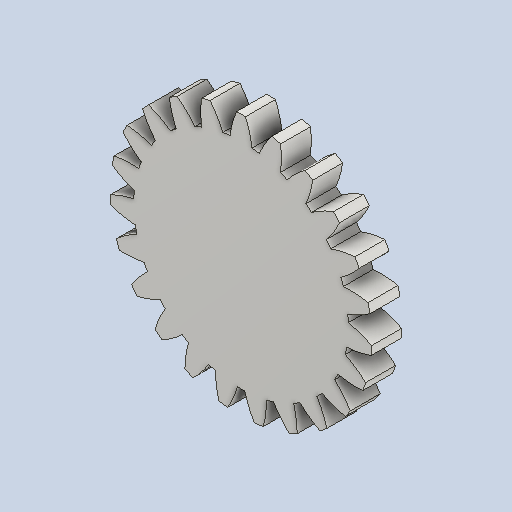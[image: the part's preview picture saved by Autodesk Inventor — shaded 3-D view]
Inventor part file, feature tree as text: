
AUTODESK INVENTOR PART (.ipt)
format: ipt  version: 2024 (Build 280153000, 153)  size: 240,640 bytes
history: native  units: mm (DEFAULTED — no unit token found)
features: plane x3, other x3, extrude x1, sketch x1
ambient origin geometry x8: Origin, YZ Plane, XZ Plane, XY Plane, X Axis, Y Axis, Z Axis, Center Point
bodies: Solid1 (feature_tree)
feature tree (8):
  extrude  "Extrusion1"  Depth=20.0mm TaperAngle=0.0deg
  plane  "Work Plane2"
  plane  "Work Plane8"
  plane  "Work Plane9"
  other  "Spur Gear"
  sketch  "Sketch1"  dims[d0=174.876705mm d1=20.0mm d2=0.0mm d3=161.0mm d4=10.0mm d5=0.0mm d16=240.0mm d17=0.0mm d34=1.36591mm d39=0.0mm d41=0.0mm d43=240.0mm d46=240.0mm d47=0.0mm d48=0.0mm]
  other  "Srf1"
  other  "Pitch Diameter"
